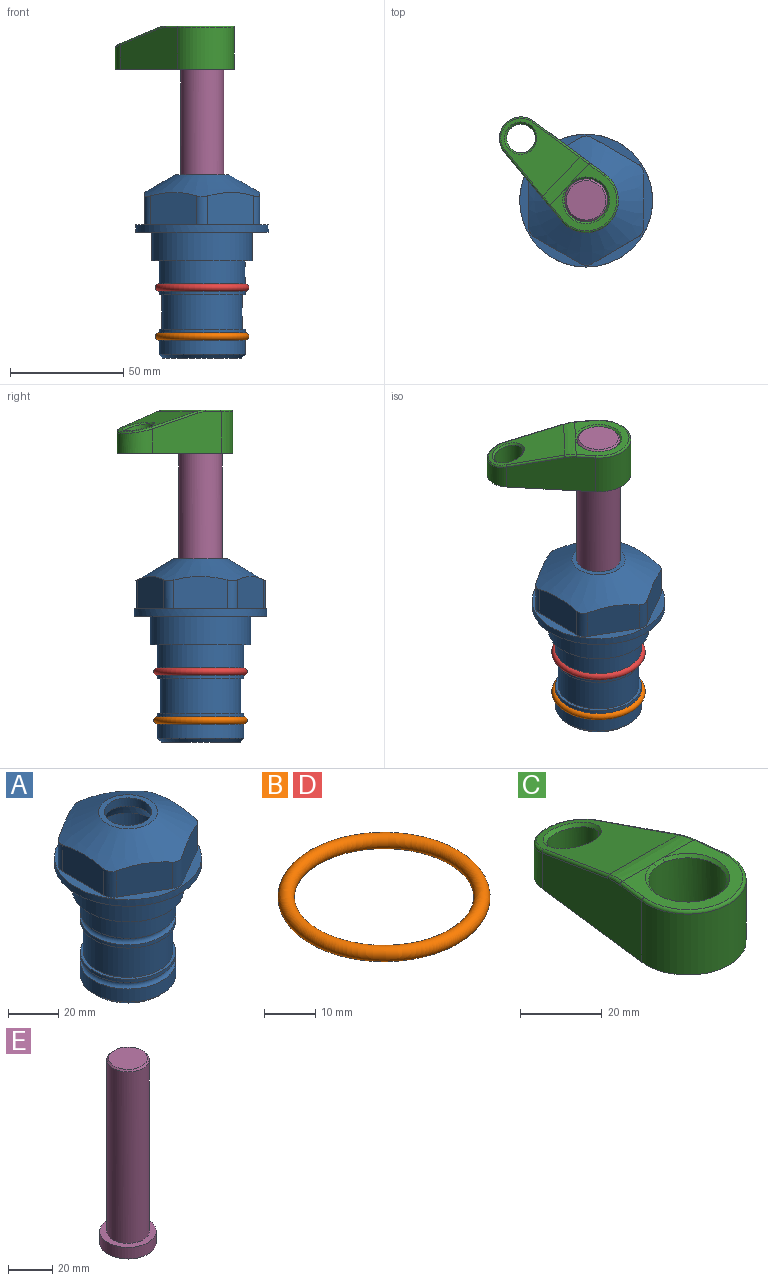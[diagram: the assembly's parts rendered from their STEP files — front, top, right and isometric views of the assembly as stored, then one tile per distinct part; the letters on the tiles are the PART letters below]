
ASSEMBLY  parts=5 mates=4
PART A: 36 faces, bbox 58.7x58.7x81 mm
  f0: cylinder r=17.78mm len=35.56mm, axis (0,0,1), area 1670.8mm2, adj f23,f24,f31
  f1: cylinder r=19.05mm len=38.1mm, axis (0,0,1), area 1191.9mm2, adj f26,f27,f30
  f2: plane 58.66x58.66mm, normal (0,0,-1), area 1150.6mm2, adj f3,f28
  f3: cylinder r=29.33mm len=58.66mm, axis (0,0,-1), area 585.1mm2, adj f2,f4
  f4: plane 58.66x58.66mm, normal (0,0,1), area 475.9mm2, adj f3,f5,f6,f7,f8,f9,f10,f11
  f5: plane 20.32x14.34mm, normal (-0.5,0.87,0), area 324.4mm2, adj f4,f15,f16,f17
  f6: plane 20.32x14.34mm, normal (0.5,0.87,0), area 324.4mm2, adj f4,f14,f15,f17
  f7: plane 23.48x14.34mm, normal (1,0,0), area 324.4mm2, adj f4,f13,f14,f17
  f8: plane 20.32x14.34mm, normal (0.5,-0.87,0), area 324.4mm2, adj f4,f12,f13,f17
  f9: plane 20.32x14.34mm, normal (-0.5,-0.87,0), area 324.4mm2, adj f4,f11,f12,f17
  f10: plane 23.48x14.34mm, normal (-1,0,0), area 324.4mm2, adj f4,f11,f16,f17
  f11: cylinder r=5.08mm len=12.85mm, axis (0,0,-1), area 67.2mm2, adj f4,f9,f10,f17
  f12: cylinder r=5.08mm len=12.85mm, axis (0,0,-1), area 67.2mm2, adj f4,f8,f9,f17
  f13: cylinder r=5.08mm len=12.85mm, axis (0,0,-1), area 67.2mm2, adj f4,f7,f8,f17
  f14: cylinder r=5.08mm len=12.85mm, axis (0,0,-1), area 67.2mm2, adj f4,f6,f7,f17
  f15: cylinder r=5.08mm len=12.85mm, axis (0,0,-1), area 67.2mm2, adj f4,f5,f6,f17
  f16: cylinder r=5.08mm len=12.85mm, axis (0,0,-1), area 67.2mm2, adj f4,f5,f10,f17
  f17: cone r=11.73mm half-angle=60deg, axis (0,0,-1), area 2071.8mm2, adj f5,f6,f7,f8,f9,f10,f11,f12
  f18: plane 23.46x23.46mm, normal (0,0,1), area 147.4mm2, adj f17,f35
  f19: plane 34.93x34.93mm, normal (0,0,-1), area 958mm2, adj f29
  f20: cylinder r=19.05mm len=38.1mm, axis (0,0,1), area 760.1mm2, adj f21,f29
  f21: torus R=19.05mm, axis (0,0,1), area 565.3mm2, adj f20,f22
  f22: cylinder r=19.05mm len=38.1mm, axis (0,0,1), area 190mm2, adj f21,f23
  f23: plane 38.1x38.1mm, normal (0,0,1), area 146.9mm2, adj f0,f22
  f24: plane 38.1x38.1mm, normal (0,0,-1), area 146.9mm2, adj f0,f25
  f25: cylinder r=19.05mm len=38.1mm, axis (0,0,1), area 190mm2, adj f24,f26
  f26: torus R=19.05mm, axis (0,0,1), area 565.3mm2, adj f1,f25
  f27: plane 44.45x44.45mm, normal (0,0,-1), area 411.7mm2, adj f1,f28
  f28: cylinder r=22.23mm len=44.45mm, axis (0,0,1), area 1773.5mm2, adj f2,f27
  f29: cone r=19.05mm half-angle=45deg, axis (0,0,1), area 257.5mm2, adj f19,f20
  f30: cylinder r=3.17mm len=6.75mm, axis (-1,0,0), area 128mm2, adj f1,f33
  f31: cylinder r=3.17mm len=6.35mm, axis (-1,0,0), area 102.5mm2, adj f0,f33
  f32: plane 25.4x25.4mm, normal (0,0,1), area 506.7mm2, adj f33
  f33: cylinder r=12.7mm len=66.42mm, axis (0,0,-1), area 5236.2mm2, adj f30,f31,f32,f34
  f34: cone r=9.53mm half-angle=30deg, axis (0,0,-1), area 443.4mm2, adj f33,f35
  f35: cylinder r=9.53mm len=19.05mm, axis (0,0,-1), area 240.9mm2, adj f18,f34
PART B: 1 faces, bbox 44.7x44.7x3.2 mm
  f0: torus R=19.05mm, axis (0,0,1), area 1193.9mm2
PART C: 31 faces, bbox 31.7x65.5x19.8 mm
  f0: plane 39.12x18.26mm, normal (0.99,0.12,0), area 612.2mm2, adj f1,f4,f7,f11,f13,f15
  f1: cylinder r=9.53mm len=18.91mm, axis (0,0,-1), area 296.1mm2, adj f0,f2,f7,f17
  f2: plane 39.12x18.26mm, normal (-0.99,0.12,0), area 612.2mm2, adj f1,f4,f7,f12,f14,f16
  f3: cylinder r=6.35mm len=12.7mm, axis (0,0,-1), area 362.4mm2, adj f7,f18
  f4: cylinder r=14.29mm len=28.58mm, axis (0,0,-1), area 882.2mm2, adj f0,f2,f7,f10
  f5: cylinder r=9.53mm len=19.05mm, axis (0,0,-1), area 1092.6mm2, adj f7,f19,f20
  f6: plane 26.99x23.69mm, normal (0,0,1), area 216.2mm2, adj f9,f10,f11,f12,f19
  f7: plane 63.5x28.58mm, normal (0,0,-1), area 661.8mm2, adj f0,f1,f2,f3,f4,f5,f22,f23
  f8: plane 33.52x23.6mm, normal (0,0.26,0.97), area 486mm2, adj f9,f15,f16,f17,f18
  f9: cylinder r=19.05mm len=24.72mm, axis (1,0,0), area 120.4mm2, adj f6,f8,f13,f14,f20
  f10: torus R=13.49mm, axis (0,0,1), area 59mm2, adj f4,f6,f11,f12
  f11: cylinder r=0.79mm len=8.67mm, axis (0.12,-0.99,0), area 10.8mm2, adj f0,f6,f10,f13
  f12: cylinder r=0.79mm len=8.67mm, axis (0.12,0.99,0), area 10.8mm2, adj f2,f6,f10,f14
  f13: bspline ~4.95x1.42mm, area 6.1mm2, adj f0,f9,f11,f15
  f14: bspline ~4.95x1.42mm, area 6.1mm2, adj f2,f9,f12,f16
  f15: cylinder r=0.79mm len=25.95mm, axis (0.12,-0.96,0.26), area 32.9mm2, adj f0,f8,f13,f17
  f16: cylinder r=0.79mm len=25.95mm, axis (0.12,0.96,-0.26), area 32.9mm2, adj f2,f8,f14,f17
  f17: bspline ~18.91x8.38mm, area 30mm2, adj f1,f8,f15,f16
  f18: bspline ~14.29x14.29mm, area 48.3mm2, adj f3,f8
  f19: cone r=9.53mm half-angle=45deg, axis (0,0,1), area 66.5mm2, adj f5,f6,f20
  f20: bspline ~3.22x0.96mm, area 3.5mm2, adj f5,f9,f19
  f21: plane 2.75x2.72mm, normal (0,0,-1), area 2.9mm2, adj f23,f25,f28
  f22: plane 23.05x15.88mm, normal (-0.99,-0.12,0), area 323.6mm2, adj f7,f25,f26,f27,f28,f29
  f23: plane 23.05x15.88mm, normal (0.99,-0.12,0), area 323.6mm2, adj f7,f21,f25,f27,f28,f30
  f24: cylinder r=9.53mm len=10.69mm, axis (0,0,-1), area 114.7mm2, adj f7,f27,f29,f30
  f25: cylinder r=12.7mm len=20.59mm, axis (0,0,-1), area 381.1mm2, adj f7,f21,f22,f23,f26,f28
  f26: plane 2.75x2.72mm, normal (0,0,-1), area 2.9mm2, adj f22,f25,f28
  f27: plane 19.72x18.37mm, normal (0,-0.26,-0.97), area 291.8mm2, adj f22,f23,f24,f28,f29,f30
  f28: cylinder r=15.88mm len=19.92mm, axis (1,0,0), area 54.8mm2, adj f21,f22,f23,f25,f26,f27
  f29: cylinder r=1.59mm len=11mm, axis (0,0,-1), area 34.7mm2, adj f7,f22,f24,f27
  f30: cylinder r=1.59mm len=11mm, axis (0,0,-1), area 34.7mm2, adj f7,f23,f24,f27
PART D: same geometry as B
PART E: 6 faces, bbox 25.4x25.4x101.6 mm
  f0: plane 17.46x17.46mm, normal (0,0,1), area 239.5mm2, adj f5
  f1: plane 25.4x25.4mm, normal (0,0,-1), area 506.7mm2, adj f2
  f2: cylinder r=12.7mm len=25.4mm, axis (0,0,1), area 506.7mm2, adj f1,f3
  f3: plane 25.4x25.4mm, normal (0,0,1), area 221.7mm2, adj f2,f4
  f4: cylinder r=9.53mm len=94.46mm, axis (0,0,1), area 5653mm2, adj f3,f5
  f5: cone r=8.73mm half-angle=45deg, axis (0,0,-1), area 64.4mm2, adj f0,f4
PLACE A at identity fixed
PLACE B t=(0,0,-21.59)mm
PLACE C rot(axis=(0,0,1),46.5deg) t=(0,0,27.55)mm
PLACE D at identity
PLACE E rot(axis=(0,0,1),46.5deg) t=(0,0,27.55)mm
MATE fastened E.f2 <-> C.f4  axis (0,0,1) through (0,0,90.26)mm
MATE fastened D.f0 <-> A.f0  axis (0,0,1) through (0,0,-24.51)mm
MATE fastened B.f0 <-> A.f0  axis (0,0,1) through (0,0,-46.1)mm
MATE cylindrical E.f2 <-> A.f0  axis (0,0,-1) through (0,0,-10.55)mm
